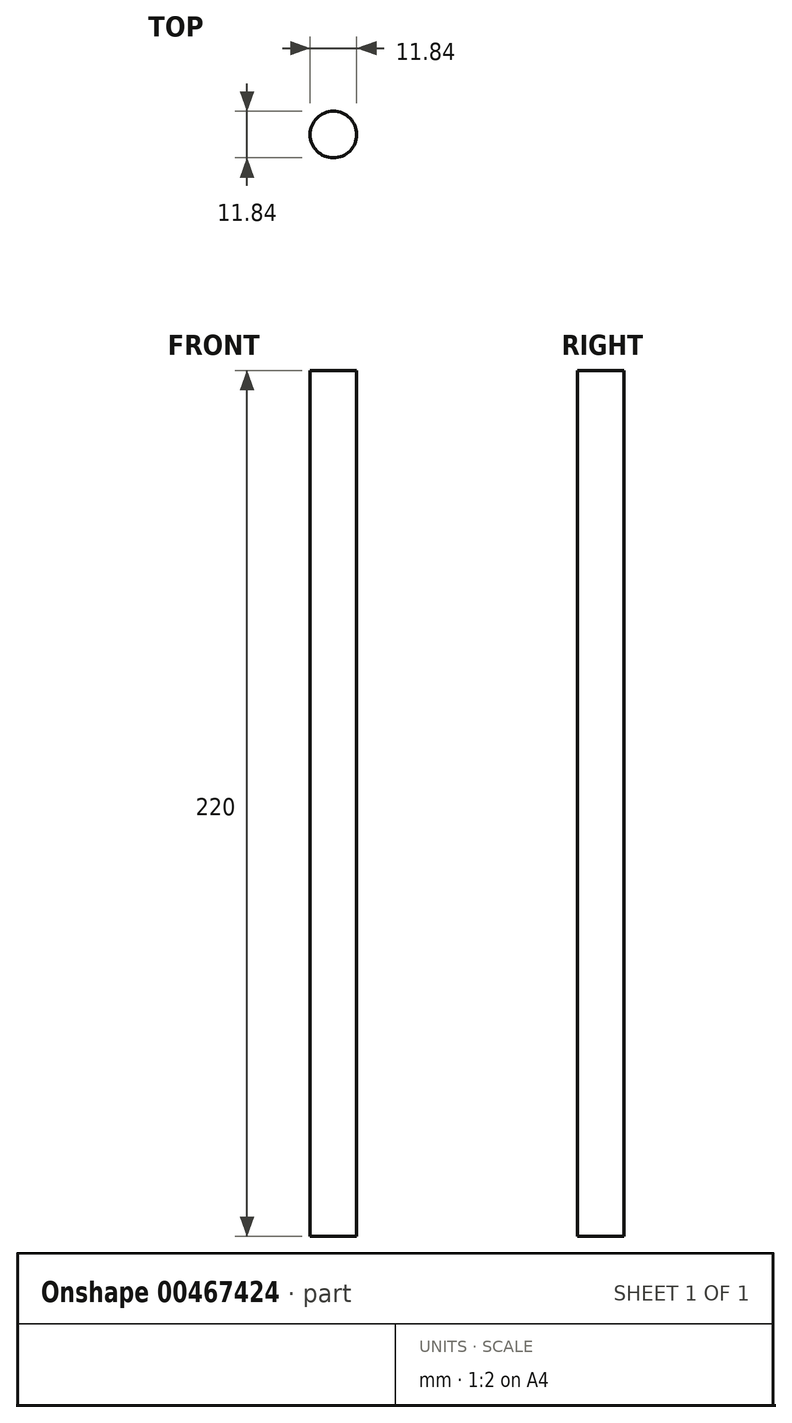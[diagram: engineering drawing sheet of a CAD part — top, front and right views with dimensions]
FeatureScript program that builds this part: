
annotation { "Feature Type Name" : "Feature", "Feature Type Description" : "" }
export const myFeature = defineFeature(function(context is Context, id is Id, definition is map)
    precondition{}
    {
        {
            var Q0;
            Q0=qCreatedBy(makeId("Top.planeOp"),FACE);
            var sketch = newSketch(context, id + "F0", { "sketchPlane" : qUnion([Q0])});
            skCircle(sketch, "E0", {"center": v(-29.3, 17.51) * mm, "radius": 5.92 * mm});
            skSolve(sketch);
        }
        {
            var Q0;
            Q0 = qSketchRegion(id + "F0", true);
            extrude(context, id + "F1", {"entities" : qUnion([Q0]), "depth" : 220 * mm});
        }
    });
